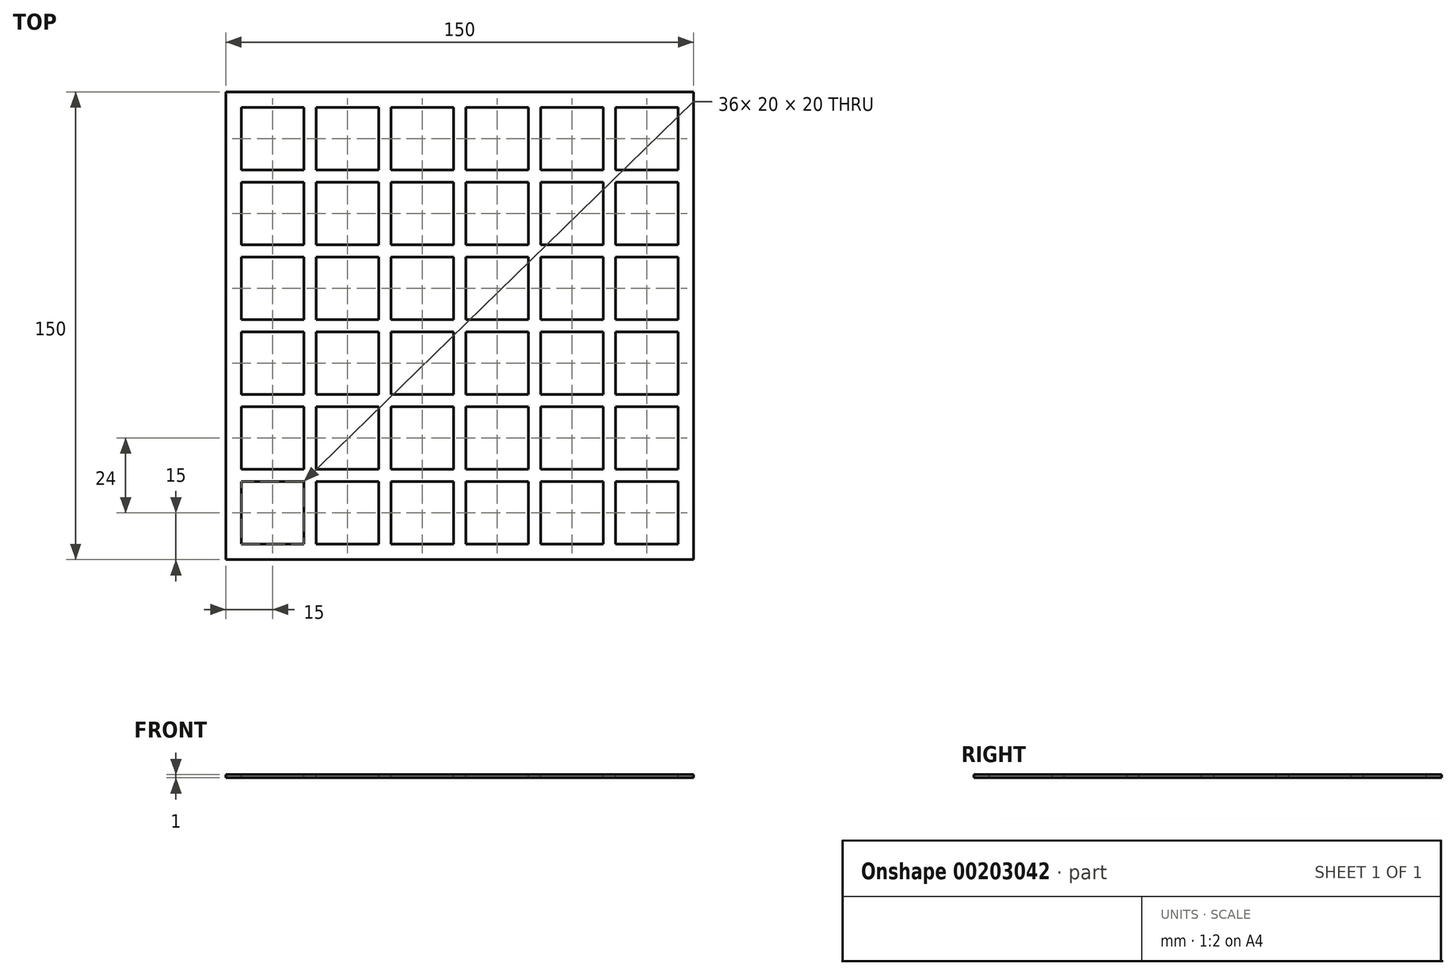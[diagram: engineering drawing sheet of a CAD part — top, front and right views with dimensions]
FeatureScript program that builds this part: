
annotation { "Feature Type Name" : "Feature", "Feature Type Description" : "" }
export const myFeature = defineFeature(function(context is Context, id is Id, definition is map)
    precondition{}
    {
        {
            var Q0;
            Q0=qCreatedBy(makeId("Top.planeOp"),FACE);
            var sketch = newSketch(context, id + "F0", { "sketchPlane" : qUnion([Q0])});
            skLineSegment(sketch, "E0.bottom", {"start": v(-75, 75) * mm, "end": v(75, 75) * mm});
            skLineSegment(sketch, "E0.top", {"start": v(-75, -75) * mm, "end": v(75, -75) * mm});
            skLineSegment(sketch, "E0.left", {"start": v(-75, 75) * mm, "end": v(-75, -75) * mm});
            skLineSegment(sketch, "E0.right", {"start": v(75, 75) * mm, "end": v(75, -75) * mm});
            skPoint(sketch, "E0.middle", {"position": v(0, 0) * mm});
            skSolve(sketch);
        }
        {
            var Q0;
            Q0 = qSketchRegion(id + "F0", true);
            extrude(context, id + "F1", {"entities" : qUnion([Q0]), "depth" : 1 * mm});
        }
        {
            var Q0;
            Q0=makeQuery(id+"F1.opExtrude","CAP_FACE",FACE,{"disambiguationData":[OSD([sQuery(id+"F0.wireOp",EDGE,"E0.bottom"),sQuery(id+"F0.wireOp",EDGE,"E0.top"),sQuery(id+"F0.wireOp",EDGE,"E0.left"),sQuery(id+"F0.wireOp",EDGE,"E0.right")])],"isStart":false});
            var sketch = newSketch(context, id + "F2", { "sketchPlane" : qUnion([Q0])});
            skLineSegment(sketch, "E1.bottom", {"start": v(-70, 70) * mm, "end": v(-50, 70) * mm});
            skLineSegment(sketch, "E1.top", {"start": v(-70, 50) * mm, "end": v(-50, 50) * mm});
            skLineSegment(sketch, "E1.left", {"start": v(-70, 70) * mm, "end": v(-70, 50) * mm});
            skLineSegment(sketch, "E1.right", {"start": v(-50, 70) * mm, "end": v(-50, 50) * mm});
            skLineSegment(sketch, "E2.1.0.0", {"start": v(-46, 70) * mm, "end": v(-26, 70) * mm});
            skLineSegment(sketch, "E2.1.0.1", {"start": v(-46, 50) * mm, "end": v(-26, 50) * mm});
            skLineSegment(sketch, "E2.1.0.2", {"start": v(-46, 70) * mm, "end": v(-46, 50) * mm});
            skLineSegment(sketch, "E2.1.0.3", {"start": v(-26, 70) * mm, "end": v(-26, 50) * mm});
            skLineSegment(sketch, "E2.2.0.0", {"start": v(-22, 70) * mm, "end": v(-2, 70) * mm});
            skLineSegment(sketch, "E2.2.0.1", {"start": v(-22, 50) * mm, "end": v(-2, 50) * mm});
            skLineSegment(sketch, "E2.2.0.2", {"start": v(-22, 70) * mm, "end": v(-22, 50) * mm});
            skLineSegment(sketch, "E2.2.0.3", {"start": v(-2, 70) * mm, "end": v(-2, 50) * mm});
            skLineSegment(sketch, "E2.3.0.0", {"start": v(2, 70) * mm, "end": v(22, 70) * mm});
            skLineSegment(sketch, "E2.3.0.1", {"start": v(2, 50) * mm, "end": v(22, 50) * mm});
            skLineSegment(sketch, "E2.3.0.2", {"start": v(2, 70) * mm, "end": v(2, 50) * mm});
            skLineSegment(sketch, "E2.3.0.3", {"start": v(22, 70) * mm, "end": v(22, 50) * mm});
            skLineSegment(sketch, "E2.4.0.0", {"start": v(26, 70) * mm, "end": v(46, 70) * mm});
            skLineSegment(sketch, "E2.4.0.1", {"start": v(26, 50) * mm, "end": v(46, 50) * mm});
            skLineSegment(sketch, "E2.4.0.2", {"start": v(26, 70) * mm, "end": v(26, 50) * mm});
            skLineSegment(sketch, "E2.4.0.3", {"start": v(46, 70) * mm, "end": v(46, 50) * mm});
            skLineSegment(sketch, "E2.5.0.0", {"start": v(50, 70) * mm, "end": v(70, 70) * mm});
            skLineSegment(sketch, "E2.5.0.1", {"start": v(50, 50) * mm, "end": v(70, 50) * mm});
            skLineSegment(sketch, "E2.5.0.2", {"start": v(50, 70) * mm, "end": v(50, 50) * mm});
            skLineSegment(sketch, "E2.5.0.3", {"start": v(70, 70) * mm, "end": v(70, 50) * mm});
            skLineSegment(sketch, "E2.direction1", {"start": v(-70, 50) * mm, "end": v(-46, 50) * mm, "construction": true});
            skLineSegment(sketch, "E3.0.1.0", {"start": v(2, 46) * mm, "end": v(22, 46) * mm});
            skLineSegment(sketch, "E3.0.1.1", {"start": v(70, 46) * mm, "end": v(70, 26) * mm});
            skLineSegment(sketch, "E3.0.1.2", {"start": v(50, 46) * mm, "end": v(50, 26) * mm});
            skLineSegment(sketch, "E3.0.1.3", {"start": v(-46, 26) * mm, "end": v(-26, 26) * mm});
            skLineSegment(sketch, "E3.0.1.4", {"start": v(-26, 46) * mm, "end": v(-26, 26) * mm});
            skLineSegment(sketch, "E3.0.1.5", {"start": v(-46, 46) * mm, "end": v(-26, 46) * mm});
            skLineSegment(sketch, "E3.0.1.6", {"start": v(-50, 46) * mm, "end": v(-50, 26) * mm});
            skLineSegment(sketch, "E3.0.1.7", {"start": v(-22, 46) * mm, "end": v(-2, 46) * mm});
            skLineSegment(sketch, "E3.0.1.8", {"start": v(-70, 46) * mm, "end": v(-70, 26) * mm});
            skLineSegment(sketch, "E3.0.1.9", {"start": v(-22, 26) * mm, "end": v(-2, 26) * mm});
            skLineSegment(sketch, "E3.0.1.10", {"start": v(26, 46) * mm, "end": v(46, 46) * mm});
            skLineSegment(sketch, "E3.0.1.11", {"start": v(-70, 46) * mm, "end": v(-50, 46) * mm});
            skLineSegment(sketch, "E3.0.1.12", {"start": v(-46, 46) * mm, "end": v(-46, 26) * mm});
            skLineSegment(sketch, "E3.0.1.13", {"start": v(26, 46) * mm, "end": v(26, 26) * mm});
            skLineSegment(sketch, "E3.0.1.14", {"start": v(50, 46) * mm, "end": v(70, 46) * mm});
            skLineSegment(sketch, "E3.0.1.15", {"start": v(-70, 26) * mm, "end": v(-46, 26) * mm, "construction": true});
            skLineSegment(sketch, "E3.0.1.16", {"start": v(50, 26) * mm, "end": v(70, 26) * mm});
            skLineSegment(sketch, "E3.0.1.17", {"start": v(46, 46) * mm, "end": v(46, 26) * mm});
            skLineSegment(sketch, "E3.0.1.18", {"start": v(26, 26) * mm, "end": v(46, 26) * mm});
            skLineSegment(sketch, "E3.0.1.19", {"start": v(2, 26) * mm, "end": v(22, 26) * mm});
            skLineSegment(sketch, "E3.0.1.20", {"start": v(2, 46) * mm, "end": v(2, 26) * mm});
            skLineSegment(sketch, "E3.0.1.21", {"start": v(22, 46) * mm, "end": v(22, 26) * mm});
            skLineSegment(sketch, "E3.0.1.22", {"start": v(-2, 46) * mm, "end": v(-2, 26) * mm});
            skLineSegment(sketch, "E3.0.1.23", {"start": v(-22, 46) * mm, "end": v(-22, 26) * mm});
            skLineSegment(sketch, "E3.0.1.24", {"start": v(-70, 26) * mm, "end": v(-50, 26) * mm});
            skLineSegment(sketch, "E3.0.2.0", {"start": v(2, 22) * mm, "end": v(22, 22) * mm});
            skLineSegment(sketch, "E3.0.2.1", {"start": v(70, 22) * mm, "end": v(70, 2) * mm});
            skLineSegment(sketch, "E3.0.2.2", {"start": v(50, 22) * mm, "end": v(50, 2) * mm});
            skLineSegment(sketch, "E3.0.2.3", {"start": v(-46, 2) * mm, "end": v(-26, 2) * mm});
            skLineSegment(sketch, "E3.0.2.4", {"start": v(-26, 22) * mm, "end": v(-26, 2) * mm});
            skLineSegment(sketch, "E3.0.2.5", {"start": v(-46, 22) * mm, "end": v(-26, 22) * mm});
            skLineSegment(sketch, "E3.0.2.6", {"start": v(-50, 22) * mm, "end": v(-50, 2) * mm});
            skLineSegment(sketch, "E3.0.2.7", {"start": v(-22, 22) * mm, "end": v(-2, 22) * mm});
            skLineSegment(sketch, "E3.0.2.8", {"start": v(-70, 22) * mm, "end": v(-70, 2) * mm});
            skLineSegment(sketch, "E3.0.2.9", {"start": v(-22, 2) * mm, "end": v(-2, 2) * mm});
            skLineSegment(sketch, "E3.0.2.10", {"start": v(26, 22) * mm, "end": v(46, 22) * mm});
            skLineSegment(sketch, "E3.0.2.11", {"start": v(-70, 22) * mm, "end": v(-50, 22) * mm});
            skLineSegment(sketch, "E3.0.2.12", {"start": v(-46, 22) * mm, "end": v(-46, 2) * mm});
            skLineSegment(sketch, "E3.0.2.13", {"start": v(26, 22) * mm, "end": v(26, 2) * mm});
            skLineSegment(sketch, "E3.0.2.14", {"start": v(50, 22) * mm, "end": v(70, 22) * mm});
            skLineSegment(sketch, "E3.0.2.15", {"start": v(-70, 2) * mm, "end": v(-46, 2) * mm, "construction": true});
            skLineSegment(sketch, "E3.0.2.16", {"start": v(50, 2) * mm, "end": v(70, 2) * mm});
            skLineSegment(sketch, "E3.0.2.17", {"start": v(46, 22) * mm, "end": v(46, 2) * mm});
            skLineSegment(sketch, "E3.0.2.18", {"start": v(26, 2) * mm, "end": v(46, 2) * mm});
            skLineSegment(sketch, "E3.0.2.19", {"start": v(2, 2) * mm, "end": v(22, 2) * mm});
            skLineSegment(sketch, "E3.0.2.20", {"start": v(2, 22) * mm, "end": v(2, 2) * mm});
            skLineSegment(sketch, "E3.0.2.21", {"start": v(22, 22) * mm, "end": v(22, 2) * mm});
            skLineSegment(sketch, "E3.0.2.22", {"start": v(-2, 22) * mm, "end": v(-2, 2) * mm});
            skLineSegment(sketch, "E3.0.2.23", {"start": v(-22, 22) * mm, "end": v(-22, 2) * mm});
            skLineSegment(sketch, "E3.0.2.24", {"start": v(-70, 2) * mm, "end": v(-50, 2) * mm});
            skLineSegment(sketch, "E3.0.3.0", {"start": v(2, -2) * mm, "end": v(22, -2) * mm});
            skLineSegment(sketch, "E3.0.3.1", {"start": v(70, -2) * mm, "end": v(70, -22) * mm});
            skLineSegment(sketch, "E3.0.3.2", {"start": v(50, -2) * mm, "end": v(50, -22) * mm});
            skLineSegment(sketch, "E3.0.3.3", {"start": v(-46, -22) * mm, "end": v(-26, -22) * mm});
            skLineSegment(sketch, "E3.0.3.4", {"start": v(-26, -2) * mm, "end": v(-26, -22) * mm});
            skLineSegment(sketch, "E3.0.3.5", {"start": v(-46, -2) * mm, "end": v(-26, -2) * mm});
            skLineSegment(sketch, "E3.0.3.6", {"start": v(-50, -2) * mm, "end": v(-50, -22) * mm});
            skLineSegment(sketch, "E3.0.3.7", {"start": v(-22, -2) * mm, "end": v(-2, -2) * mm});
            skLineSegment(sketch, "E3.0.3.8", {"start": v(-70, -2) * mm, "end": v(-70, -22) * mm});
            skLineSegment(sketch, "E3.0.3.9", {"start": v(-22, -22) * mm, "end": v(-2, -22) * mm});
            skLineSegment(sketch, "E3.0.3.10", {"start": v(26, -2) * mm, "end": v(46, -2) * mm});
            skLineSegment(sketch, "E3.0.3.11", {"start": v(-70, -2) * mm, "end": v(-50, -2) * mm});
            skLineSegment(sketch, "E3.0.3.12", {"start": v(-46, -2) * mm, "end": v(-46, -22) * mm});
            skLineSegment(sketch, "E3.0.3.13", {"start": v(26, -2) * mm, "end": v(26, -22) * mm});
            skLineSegment(sketch, "E3.0.3.14", {"start": v(50, -2) * mm, "end": v(70, -2) * mm});
            skLineSegment(sketch, "E3.0.3.15", {"start": v(-70, -22) * mm, "end": v(-46, -22) * mm, "construction": true});
            skLineSegment(sketch, "E3.0.3.16", {"start": v(50, -22) * mm, "end": v(70, -22) * mm});
            skLineSegment(sketch, "E3.0.3.17", {"start": v(46, -2) * mm, "end": v(46, -22) * mm});
            skLineSegment(sketch, "E3.0.3.18", {"start": v(26, -22) * mm, "end": v(46, -22) * mm});
            skLineSegment(sketch, "E3.0.3.19", {"start": v(2, -22) * mm, "end": v(22, -22) * mm});
            skLineSegment(sketch, "E3.0.3.20", {"start": v(2, -2) * mm, "end": v(2, -22) * mm});
            skLineSegment(sketch, "E3.0.3.21", {"start": v(22, -2) * mm, "end": v(22, -22) * mm});
            skLineSegment(sketch, "E3.0.3.22", {"start": v(-2, -2) * mm, "end": v(-2, -22) * mm});
            skLineSegment(sketch, "E3.0.3.23", {"start": v(-22, -2) * mm, "end": v(-22, -22) * mm});
            skLineSegment(sketch, "E3.0.3.24", {"start": v(-70, -22) * mm, "end": v(-50, -22) * mm});
            skLineSegment(sketch, "E3.0.4.0", {"start": v(2, -26) * mm, "end": v(22, -26) * mm});
            skLineSegment(sketch, "E3.0.4.1", {"start": v(70, -26) * mm, "end": v(70, -46) * mm});
            skLineSegment(sketch, "E3.0.4.2", {"start": v(50, -26) * mm, "end": v(50, -46) * mm});
            skLineSegment(sketch, "E3.0.4.3", {"start": v(-46, -46) * mm, "end": v(-26, -46) * mm});
            skLineSegment(sketch, "E3.0.4.4", {"start": v(-26, -26) * mm, "end": v(-26, -46) * mm});
            skLineSegment(sketch, "E3.0.4.5", {"start": v(-46, -26) * mm, "end": v(-26, -26) * mm});
            skLineSegment(sketch, "E3.0.4.6", {"start": v(-50, -26) * mm, "end": v(-50, -46) * mm});
            skLineSegment(sketch, "E3.0.4.7", {"start": v(-22, -26) * mm, "end": v(-2, -26) * mm});
            skLineSegment(sketch, "E3.0.4.8", {"start": v(-70, -26) * mm, "end": v(-70, -46) * mm});
            skLineSegment(sketch, "E3.0.4.9", {"start": v(-22, -46) * mm, "end": v(-2, -46) * mm});
            skLineSegment(sketch, "E3.0.4.10", {"start": v(26, -26) * mm, "end": v(46, -26) * mm});
            skLineSegment(sketch, "E3.0.4.11", {"start": v(-70, -26) * mm, "end": v(-50, -26) * mm});
            skLineSegment(sketch, "E3.0.4.12", {"start": v(-46, -26) * mm, "end": v(-46, -46) * mm});
            skLineSegment(sketch, "E3.0.4.13", {"start": v(26, -26) * mm, "end": v(26, -46) * mm});
            skLineSegment(sketch, "E3.0.4.14", {"start": v(50, -26) * mm, "end": v(70, -26) * mm});
            skLineSegment(sketch, "E3.0.4.15", {"start": v(-70, -46) * mm, "end": v(-46, -46) * mm, "construction": true});
            skLineSegment(sketch, "E3.0.4.16", {"start": v(50, -46) * mm, "end": v(70, -46) * mm});
            skLineSegment(sketch, "E3.0.4.17", {"start": v(46, -26) * mm, "end": v(46, -46) * mm});
            skLineSegment(sketch, "E3.0.4.18", {"start": v(26, -46) * mm, "end": v(46, -46) * mm});
            skLineSegment(sketch, "E3.0.4.19", {"start": v(2, -46) * mm, "end": v(22, -46) * mm});
            skLineSegment(sketch, "E3.0.4.20", {"start": v(2, -26) * mm, "end": v(2, -46) * mm});
            skLineSegment(sketch, "E3.0.4.21", {"start": v(22, -26) * mm, "end": v(22, -46) * mm});
            skLineSegment(sketch, "E3.0.4.22", {"start": v(-2, -26) * mm, "end": v(-2, -46) * mm});
            skLineSegment(sketch, "E3.0.4.23", {"start": v(-22, -26) * mm, "end": v(-22, -46) * mm});
            skLineSegment(sketch, "E3.0.4.24", {"start": v(-70, -46) * mm, "end": v(-50, -46) * mm});
            skLineSegment(sketch, "E3.0.5.0", {"start": v(2, -50) * mm, "end": v(22, -50) * mm});
            skLineSegment(sketch, "E3.0.5.1", {"start": v(70, -50) * mm, "end": v(70, -70) * mm});
            skLineSegment(sketch, "E3.0.5.2", {"start": v(50, -50) * mm, "end": v(50, -70) * mm});
            skLineSegment(sketch, "E3.0.5.3", {"start": v(-46, -70) * mm, "end": v(-26, -70) * mm});
            skLineSegment(sketch, "E3.0.5.4", {"start": v(-26, -50) * mm, "end": v(-26, -70) * mm});
            skLineSegment(sketch, "E3.0.5.5", {"start": v(-46, -50) * mm, "end": v(-26, -50) * mm});
            skLineSegment(sketch, "E3.0.5.6", {"start": v(-50, -50) * mm, "end": v(-50, -70) * mm});
            skLineSegment(sketch, "E3.0.5.7", {"start": v(-22, -50) * mm, "end": v(-2, -50) * mm});
            skLineSegment(sketch, "E3.0.5.8", {"start": v(-70, -50) * mm, "end": v(-70, -70) * mm});
            skLineSegment(sketch, "E3.0.5.9", {"start": v(-22, -70) * mm, "end": v(-2, -70) * mm});
            skLineSegment(sketch, "E3.0.5.10", {"start": v(26, -50) * mm, "end": v(46, -50) * mm});
            skLineSegment(sketch, "E3.0.5.11", {"start": v(-70, -50) * mm, "end": v(-50, -50) * mm});
            skLineSegment(sketch, "E3.0.5.12", {"start": v(-46, -50) * mm, "end": v(-46, -70) * mm});
            skLineSegment(sketch, "E3.0.5.13", {"start": v(26, -50) * mm, "end": v(26, -70) * mm});
            skLineSegment(sketch, "E3.0.5.14", {"start": v(50, -50) * mm, "end": v(70, -50) * mm});
            skLineSegment(sketch, "E3.0.5.15", {"start": v(-70, -70) * mm, "end": v(-46, -70) * mm, "construction": true});
            skLineSegment(sketch, "E3.0.5.16", {"start": v(50, -70) * mm, "end": v(70, -70) * mm});
            skLineSegment(sketch, "E3.0.5.17", {"start": v(46, -50) * mm, "end": v(46, -70) * mm});
            skLineSegment(sketch, "E3.0.5.18", {"start": v(26, -70) * mm, "end": v(46, -70) * mm});
            skLineSegment(sketch, "E3.0.5.19", {"start": v(2, -70) * mm, "end": v(22, -70) * mm});
            skLineSegment(sketch, "E3.0.5.20", {"start": v(2, -50) * mm, "end": v(2, -70) * mm});
            skLineSegment(sketch, "E3.0.5.21", {"start": v(22, -50) * mm, "end": v(22, -70) * mm});
            skLineSegment(sketch, "E3.0.5.22", {"start": v(-2, -50) * mm, "end": v(-2, -70) * mm});
            skLineSegment(sketch, "E3.0.5.23", {"start": v(-22, -50) * mm, "end": v(-22, -70) * mm});
            skLineSegment(sketch, "E3.0.5.24", {"start": v(-70, -70) * mm, "end": v(-50, -70) * mm});
            skLineSegment(sketch, "E3.direction1", {"start": v(-70, 50) * mm, "end": v(-70.1, 50) * mm, "construction": true});
            skLineSegment(sketch, "E3.direction2", {"start": v(-70, 50) * mm, "end": v(-70, 26) * mm, "construction": true});
            skSolve(sketch);
        }
        {
            var Q0;
            Q0 = qSketchRegion(id + "F2", true);
            extrude(context, id + "F3", {"entities" : qUnion([Q0]), "operationType" : NewBodyOperationType.REMOVE, "endBound" : BoundingType.THROUGH_ALL, "oppositeDirection" : true, "depth" : 25 * mm});
        }
    });
